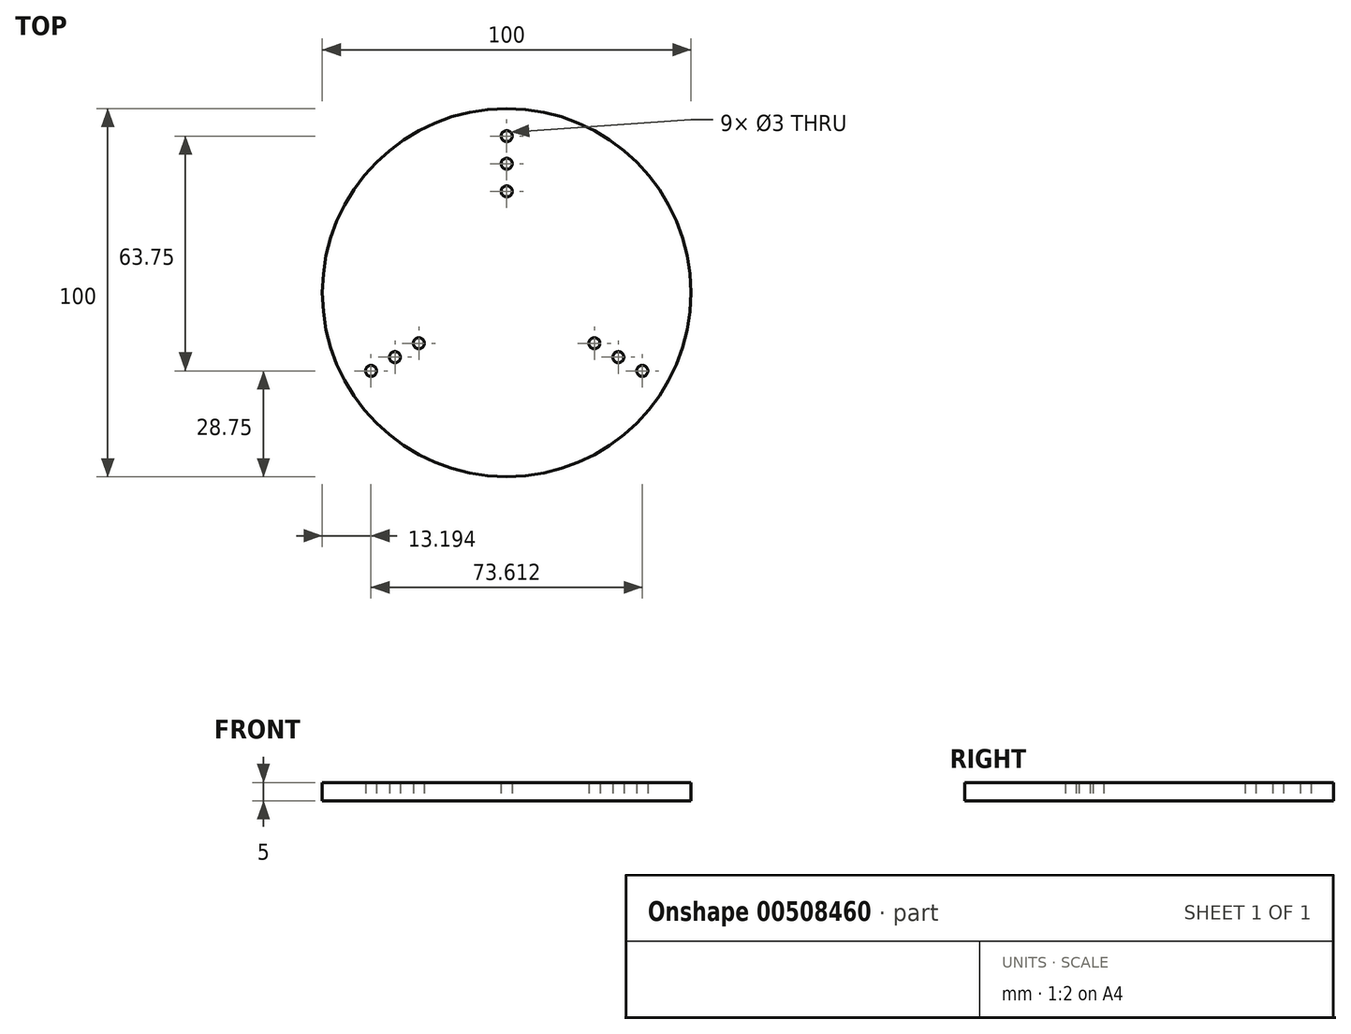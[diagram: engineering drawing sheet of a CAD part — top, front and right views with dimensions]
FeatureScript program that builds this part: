
annotation { "Feature Type Name" : "Feature", "Feature Type Description" : "" }
export const myFeature = defineFeature(function(context is Context, id is Id, definition is map)
    precondition{}
    {
        {
            var Q0;
            Q0=qCreatedBy(makeId("Top.planeOp"),FACE);
            var sketch = newSketch(context, id + "F0", { "sketchPlane" : qUnion([Q0])});
            skCircle(sketch, "E0", {"center": v(0, 0) * mm, "radius": 50 * mm});
            skCircle(sketch, "E1", {"center": v(0, 0) * mm, "radius": 42.5 * mm, "construction": true});
            skCircle(sketch, "E2", {"center": v(0, 0) * mm, "radius": 35 * mm, "construction": true});
            skCircle(sketch, "E3", {"center": v(0, 0) * mm, "radius": 27.5 * mm, "construction": true});
            skCircle(sketch, "E4", {"center": v(0, 42.5) * mm, "radius": 1.5 * mm});
            skCircle(sketch, "E5", {"center": v(0, 35) * mm, "radius": 1.5 * mm});
            skCircle(sketch, "E6", {"center": v(0, 27.5) * mm, "radius": 1.5 * mm});
            skCircle(sketch, "E7.1.0", {"center": v(-36.8, -21.25) * mm, "radius": 1.5 * mm});
            skCircle(sketch, "E7.1.1", {"center": v(-30.31, -17.5) * mm, "radius": 1.5 * mm});
            skCircle(sketch, "E7.1.2", {"center": v(-23.82, -13.75) * mm, "radius": 1.5 * mm});
            skCircle(sketch, "E7.2.0", {"center": v(36.8, -21.25) * mm, "radius": 1.5 * mm});
            skCircle(sketch, "E7.2.1", {"center": v(30.31, -17.5) * mm, "radius": 1.5 * mm});
            skCircle(sketch, "E7.2.2", {"center": v(23.82, -13.75) * mm, "radius": 1.5 * mm});
            skSolve(sketch);
        }
        {
            var Q0;
            Q0=makeQuery(id+"F0.imprint","IMPRINT",FACE,{"disambiguationData":[TD([[makeQuery(id+"F0.imprint","IMPRINT",EDGE,{"derivedFrom":sQuery(id+"F0.wireOp",EDGE,"E0")}),1.0]])]});
            extrude(context, id + "F1", {"entities" : qUnion([Q0]), "depth" : 5 * mm, "offsetDistance" : 25 * mm});
        }
    });
